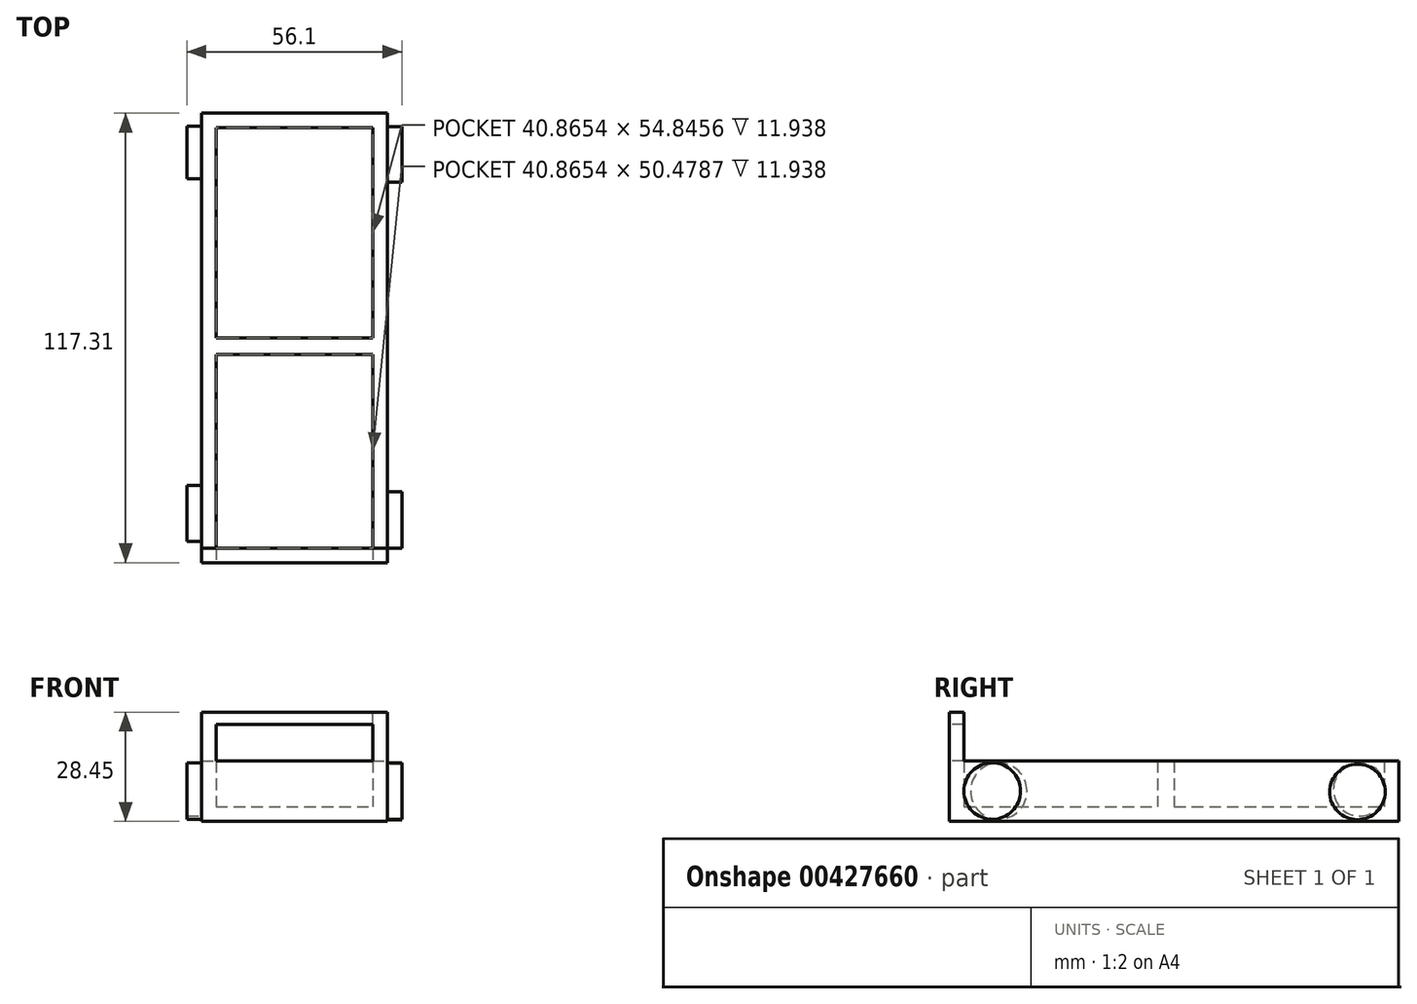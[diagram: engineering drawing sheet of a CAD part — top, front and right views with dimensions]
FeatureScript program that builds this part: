
annotation { "Feature Type Name" : "Feature", "Feature Type Description" : "" }
export const myFeature = defineFeature(function(context is Context, id is Id, definition is map)
    precondition{}
    {
        {
            var Q0;
            Q0=qCreatedBy(makeId("Top.planeOp"),FACE);
            var sketch = newSketch(context, id + "F0", { "sketchPlane" : qUnion([Q0])});
            skLineSegment(sketch, "E0.bottom", {"start": v(12.7, -47.48) * mm, "end": v(61.18, -47.48) * mm});
            skLineSegment(sketch, "E0.top", {"start": v(12.7, 69.83) * mm, "end": v(61.18, 69.83) * mm});
            skLineSegment(sketch, "E0.left", {"start": v(12.7, -47.48) * mm, "end": v(12.7, 69.83) * mm});
            skLineSegment(sketch, "E0.right", {"start": v(61.18, -47.48) * mm, "end": v(61.18, 69.83) * mm});
            skSolve(sketch);
        }
        {
            var Q0;
            Q0=makeQuery(id+"F0.imprint","IMPRINT",FACE,{"disambiguationData":[TD([[makeQuery(id+"F0.imprint","IMPRINT",EDGE,{"derivedFrom":sQuery(id+"F0.wireOp",EDGE,"E0.bottom")}),1.0]])]});
            extrude(context, id + "F1", {"entities" : qUnion([Q0]), "depth" : 15.75 * mm});
        }
        {
            var Q0;
            Q0=makeQuery(id+"F1.opExtrude","CAP_FACE",FACE,{"disambiguationData":[OSD([sQuery(id+"F0.wireOp",EDGE,"E0.bottom"),sQuery(id+"F0.wireOp",EDGE,"E0.top"),sQuery(id+"F0.wireOp",EDGE,"E0.left"),sQuery(id+"F0.wireOp",EDGE,"E0.right")])],"isStart":false});
            shell(context, id + "F2", {"entities" : qUnion([Q0]), "thickness" : 3.8 * mm});
        }
        {
            var Q0;
            Q0=makeQuery(id+"F1.opExtrude","SWEPT_FACE",FACE,{"disambiguationData":[OSD([sQuery(id+"F0.wireOp",EDGE,"E0.right")])]});
            var sketch = newSketch(context, id + "F3", { "sketchPlane" : qUnion([Q0])});
            skCircle(sketch, "E1", {"center": v(-36.32, 7.87) * mm, "radius": 7.38 * mm});
            skPoint(sketch, "E1.centerSnap0", {"position": v(-47.48, 7.87) * mm});
            skSolve(sketch);
        }
        {
            var Q0;
            Q0=makeQuery(id+"F3.imprint","IMPRINT",FACE,{"disambiguationData":[TD([[makeQuery(id+"F3.imprint","IMPRINT",EDGE,{"derivedFrom":sQuery(id+"F3.wireOp",EDGE,"E1")}),-1.0]])]});
            var sketch = newSketch(context, id + "F4", { "sketchPlane" : qUnion([Q0])});
            skCircle(sketch, "E2", {"center": v(59.01, 7.66) * mm, "radius": 7.23 * mm});
            skSolve(sketch);
        }
        {
            var Q0;
            Q0=makeQuery(id+"F3.imprint","IMPRINT",FACE,{"disambiguationData":[TD([[makeQuery(id+"F3.imprint","IMPRINT",EDGE,{"derivedFrom":sQuery(id+"F3.wireOp",EDGE,"E1")}),1.0]])]});
            extrude(context, id + "F5", {"entities" : qUnion([Q0]), "operationType" : NewBodyOperationType.ADD, "depth" : 3.8 * mm});
        }
        {
            var Q0;
            Q0 = qSketchRegion(id + "F4", true);
            extrude(context, id + "F6", {"entities" : qUnion([Q0]), "operationType" : NewBodyOperationType.ADD, "depth" : 3.8 * mm});
        }
        {
            var Q0;
            Q0=makeQuery(id+"F1.opExtrude","SWEPT_FACE",FACE,{"disambiguationData":[OSD([sQuery(id+"F0.wireOp",EDGE,"E0.left")])]});
            var sketch = newSketch(context, id + "F7", { "sketchPlane" : qUnion([Q0])});
            skCircle(sketch, "E3", {"center": v(34.61, 7.87) * mm, "radius": 7.36 * mm});
            skPoint(sketch, "E3.centerSnap0", {"position": v(47.48, 7.87) * mm});
            skSolve(sketch);
        }
        {
            var Q0;
            Q0=makeQuery(id+"F7.imprint","IMPRINT",FACE,{"disambiguationData":[TD([[makeQuery(id+"F7.imprint","IMPRINT",EDGE,{"derivedFrom":sQuery(id+"F7.wireOp",EDGE,"E3")}),-1.0]])]});
            var sketch = newSketch(context, id + "F8", { "sketchPlane" : qUnion([Q0])});
            skCircle(sketch, "E4", {"center": v(-59.58, 8.23) * mm, "radius": 6.86 * mm});
            skSolve(sketch);
        }
        {
            var Q0;
            Q0=makeQuery(id+"F8.imprint","IMPRINT",FACE,{"disambiguationData":[TD([[makeQuery(id+"F8.imprint","IMPRINT",EDGE,{"derivedFrom":sQuery(id+"F8.wireOp",EDGE,"E4")}),1.0]])]});
            extrude(context, id + "F9", {"entities" : qUnion([Q0]), "operationType" : NewBodyOperationType.ADD, "depth" : 3.8 * mm});
        }
        {
            var Q0;
            Q0 = qSketchRegion(id + "F7", true);
            extrude(context, id + "F10", {"entities" : qUnion([Q0]), "operationType" : NewBodyOperationType.ADD, "depth" : 3.8 * mm});
        }
        {
            var Q0;
            Q0=makeQuery(id+"F2.opShell","OFFSET_FACE",FACE,{"disambiguationData":[OSD([sQuery(id+"F0.wireOp",EDGE,"E0.bottom"),sQuery(id+"F0.wireOp",EDGE,"E0.top"),sQuery(id+"F0.wireOp",EDGE,"E0.left"),sQuery(id+"F0.wireOp",EDGE,"E0.right")])]});
            var sketch = newSketch(context, id + "F11", { "sketchPlane" : qUnion([Q0])});
            skLineSegment(sketch, "E5.bottom", {"start": v(16.5, 11.18) * mm, "end": v(57.37, 11.18) * mm});
            skLineSegment(sketch, "E5.top", {"start": v(16.5, 6.8) * mm, "end": v(57.37, 6.8) * mm});
            skLineSegment(sketch, "E5.left", {"start": v(16.5, 11.18) * mm, "end": v(16.5, 6.8) * mm});
            skLineSegment(sketch, "E5.right", {"start": v(57.37, 11.18) * mm, "end": v(57.37, 6.8) * mm});
            skSolve(sketch);
        }
        {
            var Q0;
            Q0 = qSketchRegion(id + "F11", true);
            extrude(context, id + "F12", {"entities" : qUnion([Q0]), "operationType" : NewBodyOperationType.ADD, "depth" : 11.94 * mm});
        }
        {
            var Q0;
            Q0=makeQuery(id+"F12.boolean.opBoolean","MERGE",FACE,{"derivedFrom":[makeQuery(id+"F1.opExtrude","CAP_FACE",FACE,{"disambiguationData":[OSD([sQuery(id+"F0.wireOp",EDGE,"E0.bottom"),sQuery(id+"F0.wireOp",EDGE,"E0.top"),sQuery(id+"F0.wireOp",EDGE,"E0.left"),sQuery(id+"F0.wireOp",EDGE,"E0.right")])],"isStart":false}),makeQuery(id+"F12.opExtrude","CAP_FACE",FACE,{"disambiguationData":[OSD([sQuery(id+"F11.wireOp",EDGE,"E5.bottom"),sQuery(id+"F11.wireOp",EDGE,"E5.top"),sQuery(id+"F11.wireOp",EDGE,"E5.left"),sQuery(id+"F11.wireOp",EDGE,"E5.right")])],"isStart":false})]});
            var sketch = newSketch(context, id + "F13", { "sketchPlane" : qUnion([Q0])});
            skLineSegment(sketch, "E6.bottom", {"start": v(12.7, -43.7) * mm, "end": v(16.5, -43.7) * mm});
            skLineSegment(sketch, "E6.top", {"start": v(12.7, -47.48) * mm, "end": v(16.5, -47.48) * mm});
            skLineSegment(sketch, "E6.left", {"start": v(12.7, -43.7) * mm, "end": v(12.7, -47.48) * mm});
            skLineSegment(sketch, "E6.right", {"start": v(16.5, -43.7) * mm, "end": v(16.5, -47.48) * mm});
            skSolve(sketch);
        }
        {
            var Q0;
            Q0 = qSketchRegion(id + "F13", true);
            extrude(context, id + "F14", {"entities" : qUnion([Q0]), "operationType" : NewBodyOperationType.ADD, "depth" : 12.7 * mm});
        }
        {
            var Q0;
            Q0=makeQuery(id+"F12.boolean.opBoolean","MERGE",FACE,{"derivedFrom":[makeQuery(id+"F1.opExtrude","CAP_FACE",FACE,{"disambiguationData":[OSD([sQuery(id+"F0.wireOp",EDGE,"E0.bottom"),sQuery(id+"F0.wireOp",EDGE,"E0.top"),sQuery(id+"F0.wireOp",EDGE,"E0.left"),sQuery(id+"F0.wireOp",EDGE,"E0.right")])],"isStart":false}),makeQuery(id+"F12.opExtrude","CAP_FACE",FACE,{"disambiguationData":[OSD([sQuery(id+"F11.wireOp",EDGE,"E5.bottom"),sQuery(id+"F11.wireOp",EDGE,"E5.top"),sQuery(id+"F11.wireOp",EDGE,"E5.left"),sQuery(id+"F11.wireOp",EDGE,"E5.right")])],"isStart":false})]});
            var sketch = newSketch(context, id + "F15", { "sketchPlane" : qUnion([Q0])});
            skLineSegment(sketch, "E7.bottom", {"start": v(57.37, -43.67) * mm, "end": v(61.18, -43.67) * mm});
            skLineSegment(sketch, "E7.top", {"start": v(57.37, -47.48) * mm, "end": v(61.18, -47.48) * mm});
            skLineSegment(sketch, "E7.left", {"start": v(57.37, -43.67) * mm, "end": v(57.37, -47.48) * mm});
            skLineSegment(sketch, "E7.right", {"start": v(61.18, -43.67) * mm, "end": v(61.18, -47.48) * mm});
            skSolve(sketch);
        }
        {
            var Q0;
            Q0 = qSketchRegion(id + "F15", true);
            extrude(context, id + "F16", {"entities" : qUnion([Q0]), "operationType" : NewBodyOperationType.ADD, "depth" : 12.7 * mm});
        }
        {
            var Q0;
            Q0=makeQuery(id+"F14.opExtrude","SWEPT_FACE",FACE,{"disambiguationData":[OSD([sQuery(id+"F13.wireOp",EDGE,"E6.right")])]});
            var sketch = newSketch(context, id + "F17", { "sketchPlane" : qUnion([Q0])});
            skLineSegment(sketch, "E8.bottom", {"start": v(-47.48, 28.45) * mm, "end": v(-43.7, 28.45) * mm});
            skLineSegment(sketch, "E8.top", {"start": v(-47.48, 25.3) * mm, "end": v(-43.7, 25.3) * mm});
            skLineSegment(sketch, "E8.left", {"start": v(-47.48, 28.45) * mm, "end": v(-47.48, 25.3) * mm});
            skLineSegment(sketch, "E8.right", {"start": v(-43.7, 28.45) * mm, "end": v(-43.7, 25.3) * mm});
            skSolve(sketch);
        }
        {
            var Q0;
            Q0 = qSketchRegion(id + "F17", true);
            extrude(context, id + "F18", {"entities" : qUnion([Q0]), "operationType" : NewBodyOperationType.ADD, "depth" : 41.9 * mm});
        }
    });
